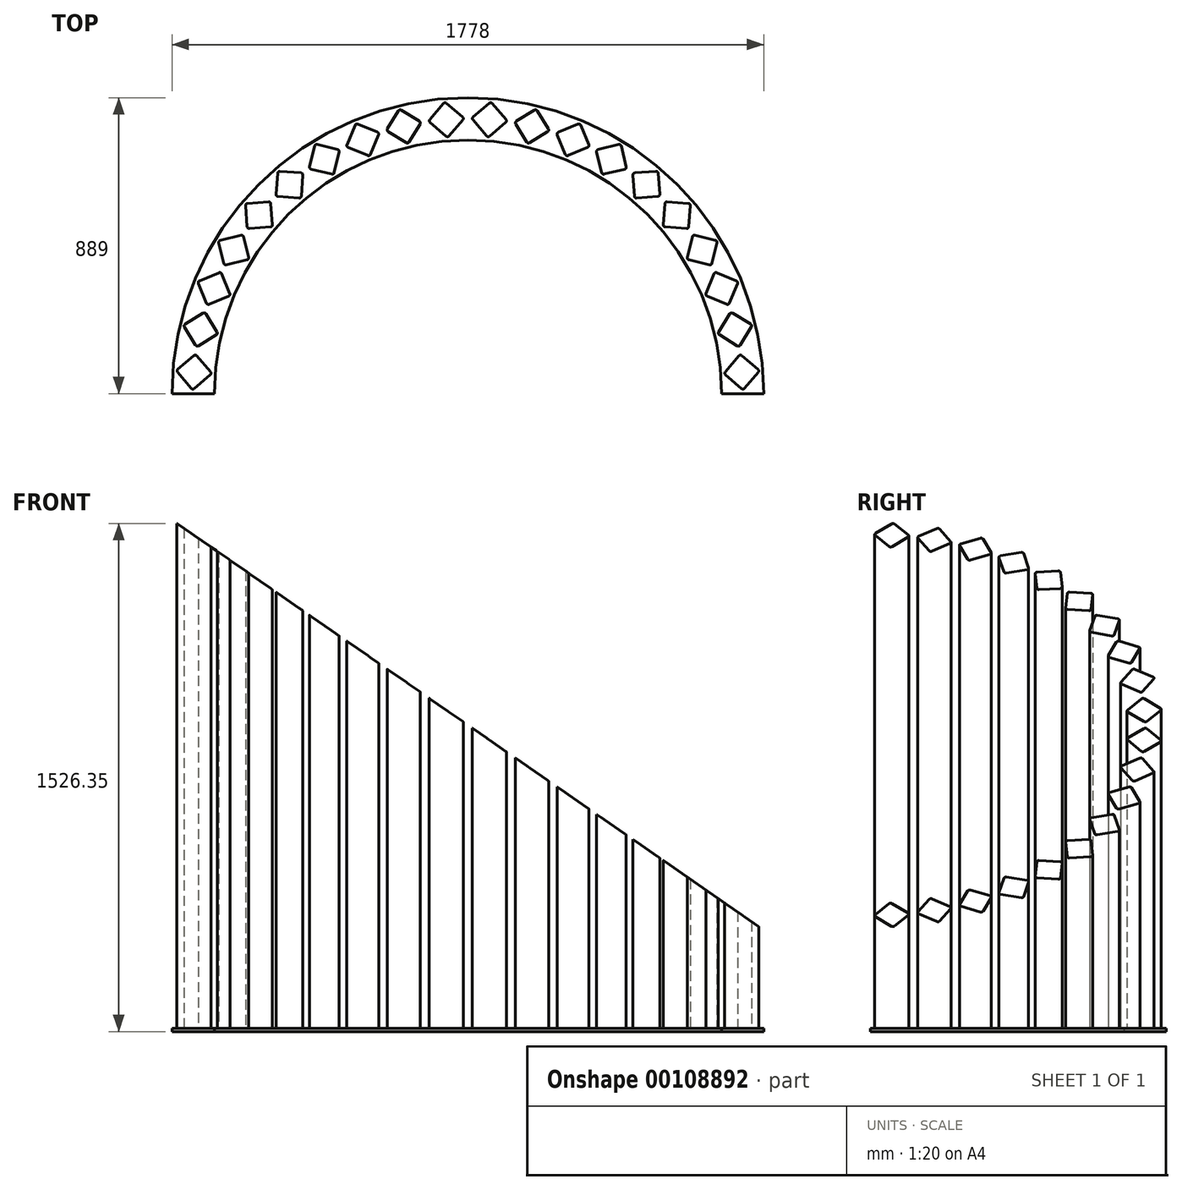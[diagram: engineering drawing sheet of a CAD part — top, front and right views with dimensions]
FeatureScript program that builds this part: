
annotation { "Feature Type Name" : "Feature", "Feature Type Description" : "" }
export const myFeature = defineFeature(function(context is Context, id is Id, definition is map)
    precondition{}
    {
        {
            var Q0;
            Q0=qCreatedBy(makeId("Top.planeOp"),FACE);
            var sketch = newSketch(context, id + "F0", { "sketchPlane" : qUnion([Q0])});
            skArc(sketch, "E0", {"start": v(889, 0) * mm, "mid": v(0, 889) * mm, "end": v(-889, 0) * mm});
            skArc(sketch, "E1", {"start": v(762, 0) * mm, "mid": v(0, 762) * mm, "end": v(-762, 0) * mm});
            skLineSegment(sketch, "E2", {"start": v(-889, 0) * mm, "end": v(-762, 0) * mm});
            skPoint(sketch, "E3.orphan", {"position": v(-1001.73, 0) * mm});
            skLineSegment(sketch, "E4.trimOffspring", {"start": v(762, 0) * mm, "end": v(889, 0) * mm});
            skSolve(sketch);
        }
        {
            var Q0;
            Q0 = qSketchRegion(id + "F0", true);
            extrude(context, id + "F1", {"entities" : qUnion([Q0]), "depth" : 9.52 * mm});
        }
        {
            var Q0;
            Q0=makeQuery(id+"F1.opExtrude","CAP_FACE",FACE,{"disambiguationData":[OSD([sQuery(id+"F0.wireOp",EDGE,"E0"),sQuery(id+"F0.wireOp",EDGE,"E1"),sQuery(id+"F0.wireOp",EDGE,"E2"),sQuery(id+"F0.wireOp",EDGE,"E4.trimOffspring")])],"isStart":false});
            var sketch = newSketch(context, id + "F2", { "sketchPlane" : qUnion([Q0])});
            skLineSegment(sketch, "E5", {"start": v(0, 0) * mm, "end": v(-951.47, 0) * mm, "construction": true});
            skLineSegment(sketch, "E6", {"start": v(0, 0) * mm, "end": v(-951.92, 74.92) * mm, "construction": true});
            skLineSegment(sketch, "E7", {"start": v(-720.22, 152.98) * mm, "end": v(-961.72, -53.27) * mm, "construction": true});
            skLineSegment(sketch, "E8", {"start": v(-871.84, 73.12) * mm, "end": v(-823.56, 114.36) * mm});
            skLineSegment(sketch, "E9", {"start": v(-822.35, 15.18) * mm, "end": v(-774.07, 56.42) * mm});
            skLineSegment(sketch, "E10", {"start": v(-814.6, 113.65) * mm, "end": v(-773.36, 65.37) * mm});
            skLineSegment(sketch, "E11", {"start": v(-872.55, 64.17) * mm, "end": v(-831.3, 15.88) * mm});
            skPoint(sketch, "E12", {"position": v(-822.96, 64.77) * mm});
            skArc(sketch, "E13.filletArc", {"start": v(-871.84, 73.12) * mm, "mid": v(-874.05, 68.79) * mm, "end": v(-872.55, 64.17) * mm});
            skArc(sketch, "E14.filletArc", {"start": v(-814.6, 113.65) * mm, "mid": v(-818.93, 115.86) * mm, "end": v(-823.56, 114.36) * mm});
            skArc(sketch, "E15.filletArc", {"start": v(-774.07, 56.42) * mm, "mid": v(-771.86, 60.75) * mm, "end": v(-773.36, 65.37) * mm});
            skArc(sketch, "E16.filletArc", {"start": v(-831.3, 15.88) * mm, "mid": v(-826.98, 13.67) * mm, "end": v(-822.35, 15.18) * mm});
            skLineSegment(sketch, "E17.9.3", {"start": v(-176.81, -755.71) * mm, "end": v(-176.81, -755.71) * mm});
            skLineSegment(sketch, "E17.9.5", {"start": v(-145.73, -818.59) * mm, "end": v(-145.73, -818.59) * mm});
            skLineSegment(sketch, "E17.10.3", {"start": v(-56.42, -774.07) * mm, "end": v(-56.42, -774.07) * mm});
            skLineSegment(sketch, "E17.12.3", {"start": v(185.55, -753.62) * mm, "end": v(185.55, -753.62) * mm});
            skLineSegment(sketch, "E17.12.7", {"start": v(199.87, -851.77) * mm, "end": v(199.87, -851.77) * mm});
            skLineSegment(sketch, "E17.14.5", {"start": v(475.78, -681.88) * mm, "end": v(475.78, -681.88) * mm});
            skLineSegment(sketch, "E17.21.0", {"start": v(872.55, 64.17) * mm, "end": v(831.3, 15.88) * mm});
            skArc(sketch, "E17.21.1", {"start": v(822.35, 15.18) * mm, "mid": v(826.98, 13.67) * mm, "end": v(831.3, 15.88) * mm});
            skLineSegment(sketch, "E17.21.2", {"start": v(822.35, 15.18) * mm, "end": v(774.07, 56.42) * mm});
            skArc(sketch, "E17.21.3", {"start": v(773.36, 65.37) * mm, "mid": v(771.86, 60.75) * mm, "end": v(774.07, 56.42) * mm});
            skLineSegment(sketch, "E17.21.4", {"start": v(814.6, 113.65) * mm, "end": v(773.36, 65.37) * mm});
            skArc(sketch, "E17.21.5", {"start": v(823.56, 114.36) * mm, "mid": v(818.93, 115.86) * mm, "end": v(814.6, 113.65) * mm});
            skLineSegment(sketch, "E17.21.6", {"start": v(871.84, 73.12) * mm, "end": v(823.56, 114.36) * mm});
            skArc(sketch, "E17.21.7", {"start": v(872.55, 64.17) * mm, "mid": v(874.05, 68.79) * mm, "end": v(871.84, 73.12) * mm});
            skLineSegment(sketch, "E17.22.0", {"start": v(851.77, 199.87) * mm, "end": v(818.59, 145.73) * mm});
            skArc(sketch, "E17.22.1", {"start": v(809.86, 143.63) * mm, "mid": v(814.66, 142.87) * mm, "end": v(818.59, 145.73) * mm});
            skLineSegment(sketch, "E17.22.2", {"start": v(809.86, 143.63) * mm, "end": v(755.71, 176.81) * mm});
            skArc(sketch, "E17.22.3", {"start": v(753.62, 185.55) * mm, "mid": v(752.86, 180.74) * mm, "end": v(755.71, 176.81) * mm});
            skLineSegment(sketch, "E17.22.4", {"start": v(786.8, 239.69) * mm, "end": v(753.62, 185.55) * mm});
            skArc(sketch, "E17.22.5", {"start": v(795.53, 241.78) * mm, "mid": v(790.73, 242.54) * mm, "end": v(786.8, 239.69) * mm});
            skLineSegment(sketch, "E17.22.6", {"start": v(849.67, 208.6) * mm, "end": v(795.53, 241.78) * mm});
            skArc(sketch, "E17.22.7", {"start": v(851.77, 199.87) * mm, "mid": v(852.53, 204.67) * mm, "end": v(849.67, 208.6) * mm});
            skLineSegment(sketch, "E17.23.0", {"start": v(810.01, 330.66) * mm, "end": v(785.71, 272) * mm});
            skArc(sketch, "E17.23.1", {"start": v(777.42, 268.56) * mm, "mid": v(782.28, 268.56) * mm, "end": v(785.71, 272) * mm});
            skLineSegment(sketch, "E17.23.2", {"start": v(777.42, 268.56) * mm, "end": v(718.75, 292.86) * mm});
            skArc(sketch, "E17.23.3", {"start": v(715.31, 301.15) * mm, "mid": v(715.31, 296.3) * mm, "end": v(718.75, 292.86) * mm});
            skLineSegment(sketch, "E17.23.4", {"start": v(739.61, 359.82) * mm, "end": v(715.31, 301.15) * mm});
            skArc(sketch, "E17.23.5", {"start": v(747.9, 363.26) * mm, "mid": v(743.05, 363.26) * mm, "end": v(739.61, 359.82) * mm});
            skLineSegment(sketch, "E17.23.6", {"start": v(806.58, 338.95) * mm, "end": v(747.9, 363.26) * mm});
            skArc(sketch, "E17.23.7", {"start": v(810.01, 330.66) * mm, "mid": v(810.01, 335.52) * mm, "end": v(806.58, 338.95) * mm});
            skLineSegment(sketch, "E17.24.0", {"start": v(748.31, 453.3) * mm, "end": v(733.49, 391.56) * mm});
            skArc(sketch, "E17.24.1", {"start": v(725.83, 386.86) * mm, "mid": v(730.63, 387.62) * mm, "end": v(733.49, 391.56) * mm});
            skLineSegment(sketch, "E17.24.2", {"start": v(725.83, 386.86) * mm, "end": v(664.09, 401.69) * mm});
            skArc(sketch, "E17.24.3", {"start": v(659.4, 409.34) * mm, "mid": v(660.16, 404.54) * mm, "end": v(664.09, 401.69) * mm});
            skLineSegment(sketch, "E17.24.4", {"start": v(674.22, 471.09) * mm, "end": v(659.4, 409.34) * mm});
            skArc(sketch, "E17.24.5", {"start": v(681.88, 475.78) * mm, "mid": v(677.08, 475.02) * mm, "end": v(674.22, 471.09) * mm});
            skLineSegment(sketch, "E17.24.6", {"start": v(743.62, 460.96) * mm, "end": v(681.88, 475.78) * mm});
            skArc(sketch, "E17.24.7", {"start": v(748.31, 453.3) * mm, "mid": v(747.55, 458.1) * mm, "end": v(743.62, 460.96) * mm});
            skLineSegment(sketch, "E17.25.0", {"start": v(668.19, 564.78) * mm, "end": v(663.2, 501.48) * mm});
            skArc(sketch, "E17.25.1", {"start": v(656.38, 495.65) * mm, "mid": v(661, 497.15) * mm, "end": v(663.2, 501.48) * mm});
            skLineSegment(sketch, "E17.25.2", {"start": v(656.38, 495.65) * mm, "end": v(593.07, 500.63) * mm});
            skArc(sketch, "E17.25.3", {"start": v(587.24, 507.46) * mm, "mid": v(588.74, 502.83) * mm, "end": v(593.07, 500.63) * mm});
            skLineSegment(sketch, "E17.25.4", {"start": v(592.22, 570.76) * mm, "end": v(587.24, 507.46) * mm});
            skArc(sketch, "E17.25.5", {"start": v(599.05, 576.6) * mm, "mid": v(594.43, 575.1) * mm, "end": v(592.22, 570.76) * mm});
            skLineSegment(sketch, "E17.25.6", {"start": v(662.36, 571.61) * mm, "end": v(599.05, 576.6) * mm});
            skArc(sketch, "E17.25.7", {"start": v(668.19, 564.78) * mm, "mid": v(666.69, 569.4) * mm, "end": v(662.36, 571.61) * mm});
            skLineSegment(sketch, "E17.26.0", {"start": v(571.61, 662.36) * mm, "end": v(576.6, 599.05) * mm});
            skArc(sketch, "E17.26.1", {"start": v(570.76, 592.22) * mm, "mid": v(575.1, 594.43) * mm, "end": v(576.6, 599.05) * mm});
            skLineSegment(sketch, "E17.26.2", {"start": v(570.76, 592.22) * mm, "end": v(507.46, 587.24) * mm});
            skArc(sketch, "E17.26.3", {"start": v(500.63, 593.07) * mm, "mid": v(502.83, 588.74) * mm, "end": v(507.46, 587.24) * mm});
            skLineSegment(sketch, "E17.26.4", {"start": v(495.65, 656.38) * mm, "end": v(500.63, 593.07) * mm});
            skArc(sketch, "E17.26.5", {"start": v(501.48, 663.2) * mm, "mid": v(497.15, 661) * mm, "end": v(495.65, 656.38) * mm});
            skLineSegment(sketch, "E17.26.6", {"start": v(564.78, 668.19) * mm, "end": v(501.48, 663.2) * mm});
            skArc(sketch, "E17.26.7", {"start": v(571.61, 662.36) * mm, "mid": v(569.4, 666.69) * mm, "end": v(564.78, 668.19) * mm});
            skLineSegment(sketch, "E17.27.0", {"start": v(460.96, 743.62) * mm, "end": v(475.78, 681.88) * mm});
            skArc(sketch, "E17.27.1", {"start": v(471.09, 674.22) * mm, "mid": v(475.02, 677.08) * mm, "end": v(475.78, 681.88) * mm});
            skLineSegment(sketch, "E17.27.2", {"start": v(471.09, 674.22) * mm, "end": v(409.34, 659.4) * mm});
            skArc(sketch, "E17.27.3", {"start": v(401.69, 664.09) * mm, "mid": v(404.54, 660.16) * mm, "end": v(409.34, 659.4) * mm});
            skLineSegment(sketch, "E17.27.4", {"start": v(386.86, 725.83) * mm, "end": v(401.69, 664.09) * mm});
            skArc(sketch, "E17.27.5", {"start": v(391.56, 733.49) * mm, "mid": v(387.62, 730.63) * mm, "end": v(386.86, 725.83) * mm});
            skLineSegment(sketch, "E17.27.6", {"start": v(453.3, 748.31) * mm, "end": v(391.56, 733.49) * mm});
            skArc(sketch, "E17.27.7", {"start": v(460.96, 743.62) * mm, "mid": v(458.1, 747.55) * mm, "end": v(453.3, 748.31) * mm});
            skLineSegment(sketch, "E17.28.0", {"start": v(338.95, 806.58) * mm, "end": v(363.26, 747.9) * mm});
            skArc(sketch, "E17.28.1", {"start": v(359.82, 739.61) * mm, "mid": v(363.26, 743.05) * mm, "end": v(363.26, 747.9) * mm});
            skLineSegment(sketch, "E17.28.2", {"start": v(359.82, 739.61) * mm, "end": v(301.15, 715.31) * mm});
            skArc(sketch, "E17.28.3", {"start": v(292.86, 718.75) * mm, "mid": v(296.3, 715.31) * mm, "end": v(301.15, 715.31) * mm});
            skLineSegment(sketch, "E17.28.4", {"start": v(268.56, 777.42) * mm, "end": v(292.86, 718.75) * mm});
            skArc(sketch, "E17.28.5", {"start": v(272, 785.71) * mm, "mid": v(268.56, 782.28) * mm, "end": v(268.56, 777.42) * mm});
            skLineSegment(sketch, "E17.28.6", {"start": v(330.66, 810.01) * mm, "end": v(272, 785.71) * mm});
            skArc(sketch, "E17.28.7", {"start": v(338.95, 806.58) * mm, "mid": v(335.52, 810.01) * mm, "end": v(330.66, 810.01) * mm});
            skLineSegment(sketch, "E17.29.0", {"start": v(208.6, 849.67) * mm, "end": v(241.78, 795.53) * mm});
            skArc(sketch, "E17.29.1", {"start": v(239.69, 786.8) * mm, "mid": v(242.54, 790.73) * mm, "end": v(241.78, 795.53) * mm});
            skLineSegment(sketch, "E17.29.2", {"start": v(239.69, 786.8) * mm, "end": v(185.55, 753.62) * mm});
            skArc(sketch, "E17.29.3", {"start": v(176.81, 755.71) * mm, "mid": v(180.74, 752.86) * mm, "end": v(185.55, 753.62) * mm});
            skLineSegment(sketch, "E17.29.4", {"start": v(143.63, 809.86) * mm, "end": v(176.81, 755.71) * mm});
            skArc(sketch, "E17.29.5", {"start": v(145.73, 818.59) * mm, "mid": v(142.87, 814.66) * mm, "end": v(143.63, 809.86) * mm});
            skLineSegment(sketch, "E17.29.6", {"start": v(199.87, 851.77) * mm, "end": v(145.73, 818.59) * mm});
            skArc(sketch, "E17.29.7", {"start": v(208.6, 849.67) * mm, "mid": v(204.67, 852.53) * mm, "end": v(199.87, 851.77) * mm});
            skLineSegment(sketch, "E17.30.0", {"start": v(73.12, 871.84) * mm, "end": v(114.36, 823.56) * mm});
            skArc(sketch, "E17.30.1", {"start": v(113.65, 814.6) * mm, "mid": v(115.86, 818.93) * mm, "end": v(114.36, 823.56) * mm});
            skLineSegment(sketch, "E17.30.2", {"start": v(113.65, 814.6) * mm, "end": v(65.37, 773.36) * mm});
            skArc(sketch, "E17.30.3", {"start": v(56.42, 774.07) * mm, "mid": v(60.75, 771.86) * mm, "end": v(65.37, 773.36) * mm});
            skLineSegment(sketch, "E17.30.4", {"start": v(15.18, 822.35) * mm, "end": v(56.42, 774.07) * mm});
            skArc(sketch, "E17.30.5", {"start": v(15.88, 831.3) * mm, "mid": v(13.67, 826.98) * mm, "end": v(15.18, 822.35) * mm});
            skLineSegment(sketch, "E17.30.6", {"start": v(64.17, 872.55) * mm, "end": v(15.88, 831.3) * mm});
            skArc(sketch, "E17.30.7", {"start": v(73.12, 871.84) * mm, "mid": v(68.79, 874.05) * mm, "end": v(64.17, 872.55) * mm});
            skLineSegment(sketch, "E17.31.0", {"start": v(-64.17, 872.55) * mm, "end": v(-15.88, 831.3) * mm});
            skArc(sketch, "E17.31.1", {"start": v(-15.18, 822.35) * mm, "mid": v(-13.67, 826.98) * mm, "end": v(-15.88, 831.3) * mm});
            skLineSegment(sketch, "E17.31.2", {"start": v(-15.18, 822.35) * mm, "end": v(-56.42, 774.07) * mm});
            skArc(sketch, "E17.31.3", {"start": v(-65.37, 773.36) * mm, "mid": v(-60.75, 771.86) * mm, "end": v(-56.42, 774.07) * mm});
            skLineSegment(sketch, "E17.31.4", {"start": v(-113.65, 814.6) * mm, "end": v(-65.37, 773.36) * mm});
            skArc(sketch, "E17.31.5", {"start": v(-114.36, 823.56) * mm, "mid": v(-115.86, 818.93) * mm, "end": v(-113.65, 814.6) * mm});
            skLineSegment(sketch, "E17.31.6", {"start": v(-73.12, 871.84) * mm, "end": v(-114.36, 823.56) * mm});
            skArc(sketch, "E17.31.7", {"start": v(-64.17, 872.55) * mm, "mid": v(-68.79, 874.05) * mm, "end": v(-73.12, 871.84) * mm});
            skLineSegment(sketch, "E17.32.0", {"start": v(-199.87, 851.77) * mm, "end": v(-145.73, 818.59) * mm});
            skArc(sketch, "E17.32.1", {"start": v(-143.63, 809.86) * mm, "mid": v(-142.87, 814.66) * mm, "end": v(-145.73, 818.59) * mm});
            skLineSegment(sketch, "E17.32.2", {"start": v(-143.63, 809.86) * mm, "end": v(-176.81, 755.71) * mm});
            skArc(sketch, "E17.32.3", {"start": v(-185.55, 753.62) * mm, "mid": v(-180.74, 752.86) * mm, "end": v(-176.81, 755.71) * mm});
            skLineSegment(sketch, "E17.32.4", {"start": v(-239.69, 786.8) * mm, "end": v(-185.55, 753.62) * mm});
            skArc(sketch, "E17.32.5", {"start": v(-241.78, 795.53) * mm, "mid": v(-242.54, 790.73) * mm, "end": v(-239.69, 786.8) * mm});
            skLineSegment(sketch, "E17.32.6", {"start": v(-208.6, 849.67) * mm, "end": v(-241.78, 795.53) * mm});
            skArc(sketch, "E17.32.7", {"start": v(-199.87, 851.77) * mm, "mid": v(-204.67, 852.53) * mm, "end": v(-208.6, 849.67) * mm});
            skLineSegment(sketch, "E17.33.0", {"start": v(-330.66, 810.01) * mm, "end": v(-272, 785.71) * mm});
            skArc(sketch, "E17.33.1", {"start": v(-268.56, 777.42) * mm, "mid": v(-268.56, 782.28) * mm, "end": v(-272, 785.71) * mm});
            skLineSegment(sketch, "E17.33.2", {"start": v(-268.56, 777.42) * mm, "end": v(-292.86, 718.75) * mm});
            skArc(sketch, "E17.33.3", {"start": v(-301.15, 715.31) * mm, "mid": v(-296.3, 715.31) * mm, "end": v(-292.86, 718.75) * mm});
            skLineSegment(sketch, "E17.33.4", {"start": v(-359.82, 739.61) * mm, "end": v(-301.15, 715.31) * mm});
            skArc(sketch, "E17.33.5", {"start": v(-363.26, 747.9) * mm, "mid": v(-363.26, 743.05) * mm, "end": v(-359.82, 739.61) * mm});
            skLineSegment(sketch, "E17.33.6", {"start": v(-338.95, 806.58) * mm, "end": v(-363.26, 747.9) * mm});
            skArc(sketch, "E17.33.7", {"start": v(-330.66, 810.01) * mm, "mid": v(-335.52, 810.01) * mm, "end": v(-338.95, 806.58) * mm});
            skLineSegment(sketch, "E17.34.0", {"start": v(-453.3, 748.31) * mm, "end": v(-391.56, 733.49) * mm});
            skArc(sketch, "E17.34.1", {"start": v(-386.86, 725.83) * mm, "mid": v(-387.62, 730.63) * mm, "end": v(-391.56, 733.49) * mm});
            skLineSegment(sketch, "E17.34.2", {"start": v(-386.86, 725.83) * mm, "end": v(-401.69, 664.09) * mm});
            skArc(sketch, "E17.34.3", {"start": v(-409.34, 659.4) * mm, "mid": v(-404.54, 660.16) * mm, "end": v(-401.69, 664.09) * mm});
            skLineSegment(sketch, "E17.34.4", {"start": v(-471.09, 674.22) * mm, "end": v(-409.34, 659.4) * mm});
            skArc(sketch, "E17.34.5", {"start": v(-475.78, 681.88) * mm, "mid": v(-475.02, 677.08) * mm, "end": v(-471.09, 674.22) * mm});
            skLineSegment(sketch, "E17.34.6", {"start": v(-460.96, 743.62) * mm, "end": v(-475.78, 681.88) * mm});
            skArc(sketch, "E17.34.7", {"start": v(-453.3, 748.31) * mm, "mid": v(-458.1, 747.55) * mm, "end": v(-460.96, 743.62) * mm});
            skLineSegment(sketch, "E17.35.0", {"start": v(-564.78, 668.19) * mm, "end": v(-501.48, 663.2) * mm});
            skArc(sketch, "E17.35.1", {"start": v(-495.65, 656.38) * mm, "mid": v(-497.15, 661) * mm, "end": v(-501.48, 663.2) * mm});
            skLineSegment(sketch, "E17.35.2", {"start": v(-495.65, 656.38) * mm, "end": v(-500.63, 593.07) * mm});
            skArc(sketch, "E17.35.3", {"start": v(-507.46, 587.24) * mm, "mid": v(-502.83, 588.74) * mm, "end": v(-500.63, 593.07) * mm});
            skLineSegment(sketch, "E17.35.4", {"start": v(-570.76, 592.22) * mm, "end": v(-507.46, 587.24) * mm});
            skArc(sketch, "E17.35.5", {"start": v(-576.6, 599.05) * mm, "mid": v(-575.1, 594.43) * mm, "end": v(-570.76, 592.22) * mm});
            skLineSegment(sketch, "E17.35.6", {"start": v(-571.61, 662.36) * mm, "end": v(-576.6, 599.05) * mm});
            skArc(sketch, "E17.35.7", {"start": v(-564.78, 668.19) * mm, "mid": v(-569.4, 666.69) * mm, "end": v(-571.61, 662.36) * mm});
            skLineSegment(sketch, "E17.36.0", {"start": v(-662.36, 571.61) * mm, "end": v(-599.05, 576.6) * mm});
            skArc(sketch, "E17.36.1", {"start": v(-592.22, 570.76) * mm, "mid": v(-594.43, 575.1) * mm, "end": v(-599.05, 576.6) * mm});
            skLineSegment(sketch, "E17.36.2", {"start": v(-592.22, 570.76) * mm, "end": v(-587.24, 507.46) * mm});
            skArc(sketch, "E17.36.3", {"start": v(-593.07, 500.63) * mm, "mid": v(-588.74, 502.83) * mm, "end": v(-587.24, 507.46) * mm});
            skLineSegment(sketch, "E17.36.4", {"start": v(-656.38, 495.65) * mm, "end": v(-593.07, 500.63) * mm});
            skArc(sketch, "E17.36.5", {"start": v(-663.2, 501.48) * mm, "mid": v(-661, 497.15) * mm, "end": v(-656.38, 495.65) * mm});
            skLineSegment(sketch, "E17.36.6", {"start": v(-668.19, 564.78) * mm, "end": v(-663.2, 501.48) * mm});
            skArc(sketch, "E17.36.7", {"start": v(-662.36, 571.61) * mm, "mid": v(-666.69, 569.4) * mm, "end": v(-668.19, 564.78) * mm});
            skLineSegment(sketch, "E17.37.0", {"start": v(-743.62, 460.96) * mm, "end": v(-681.88, 475.78) * mm});
            skArc(sketch, "E17.37.1", {"start": v(-674.22, 471.09) * mm, "mid": v(-677.08, 475.02) * mm, "end": v(-681.88, 475.78) * mm});
            skLineSegment(sketch, "E17.37.2", {"start": v(-674.22, 471.09) * mm, "end": v(-659.4, 409.34) * mm});
            skArc(sketch, "E17.37.3", {"start": v(-664.09, 401.69) * mm, "mid": v(-660.16, 404.54) * mm, "end": v(-659.4, 409.34) * mm});
            skLineSegment(sketch, "E17.37.4", {"start": v(-725.83, 386.86) * mm, "end": v(-664.09, 401.69) * mm});
            skArc(sketch, "E17.37.5", {"start": v(-733.49, 391.56) * mm, "mid": v(-730.63, 387.62) * mm, "end": v(-725.83, 386.86) * mm});
            skLineSegment(sketch, "E17.37.6", {"start": v(-748.31, 453.3) * mm, "end": v(-733.49, 391.56) * mm});
            skArc(sketch, "E17.37.7", {"start": v(-743.62, 460.96) * mm, "mid": v(-747.55, 458.1) * mm, "end": v(-748.31, 453.3) * mm});
            skLineSegment(sketch, "E17.38.0", {"start": v(-806.58, 338.95) * mm, "end": v(-747.9, 363.26) * mm});
            skArc(sketch, "E17.38.1", {"start": v(-739.61, 359.82) * mm, "mid": v(-743.05, 363.26) * mm, "end": v(-747.9, 363.26) * mm});
            skLineSegment(sketch, "E17.38.2", {"start": v(-739.61, 359.82) * mm, "end": v(-715.31, 301.15) * mm});
            skArc(sketch, "E17.38.3", {"start": v(-718.75, 292.86) * mm, "mid": v(-715.31, 296.3) * mm, "end": v(-715.31, 301.15) * mm});
            skLineSegment(sketch, "E17.38.4", {"start": v(-777.42, 268.56) * mm, "end": v(-718.75, 292.86) * mm});
            skArc(sketch, "E17.38.5", {"start": v(-785.71, 272) * mm, "mid": v(-782.28, 268.56) * mm, "end": v(-777.42, 268.56) * mm});
            skLineSegment(sketch, "E17.38.6", {"start": v(-810.01, 330.66) * mm, "end": v(-785.71, 272) * mm});
            skArc(sketch, "E17.38.7", {"start": v(-806.58, 338.95) * mm, "mid": v(-810.01, 335.52) * mm, "end": v(-810.01, 330.66) * mm});
            skPoint(sketch, "E17.center", {"position": v(0, 0) * mm});
            skLineSegment(sketch, "E18.1.39.0", {"start": v(-849.67, 208.6) * mm, "end": v(-795.53, 241.78) * mm});
            skArc(sketch, "E18.3.39.0", {"start": v(-786.8, 239.69) * mm, "mid": v(-790.73, 242.54) * mm, "end": v(-795.53, 241.78) * mm});
            skLineSegment(sketch, "E18.7.39.0", {"start": v(-786.8, 239.69) * mm, "end": v(-753.62, 185.55) * mm});
            skArc(sketch, "E18.10.39.0", {"start": v(-755.71, 176.81) * mm, "mid": v(-752.86, 180.74) * mm, "end": v(-753.62, 185.55) * mm});
            skLineSegment(sketch, "E18.14.39.0", {"start": v(-809.86, 143.63) * mm, "end": v(-755.71, 176.81) * mm});
            skArc(sketch, "E18.17.39.0", {"start": v(-818.59, 145.73) * mm, "mid": v(-814.66, 142.87) * mm, "end": v(-809.86, 143.63) * mm});
            skLineSegment(sketch, "E18.21.39.0", {"start": v(-851.77, 199.87) * mm, "end": v(-818.59, 145.73) * mm});
            skArc(sketch, "E18.24.39.0", {"start": v(-849.67, 208.6) * mm, "mid": v(-852.53, 204.67) * mm, "end": v(-851.77, 199.87) * mm});
            skPoint(sketch, "E19.orphan", {"position": v(-831.3, -15.88) * mm});
            skArc(sketch, "E20.trimOffspring", {"start": v(825.39, 13.75) * mm, "mid": v(-6.88, 825.47) * mm, "end": v(-825.5, 0) * mm, "construction": true});
            skPoint(sketch, "E21.orphan", {"position": v(-747.9, -363.26) * mm});
            skPoint(sketch, "E22.orphan", {"position": v(-185.55, -753.62) * mm});
            skPoint(sketch, "E23.orphan", {"position": v(-143.63, -809.86) * mm});
            skPoint(sketch, "E24.orphan", {"position": v(-65.37, -773.36) * mm});
            skPoint(sketch, "E25.orphan", {"position": v(176.81, -755.71) * mm});
            skPoint(sketch, "E26.orphan", {"position": v(208.6, -849.67) * mm});
            skPoint(sketch, "E27.orphan", {"position": v(471.09, -674.22) * mm});
            skPoint(sketch, "E28", {"position": v(-13.67, 826.98) * mm});
            skPoint(sketch, "E29", {"position": v(13.65, 826.9) * mm});
            skSolve(sketch);
        }
        {
            var Q0;
            Q0 = qSketchRegion(id + "F2", true);
            extrude(context, id + "F3", {"entities" : qUnion([Q0]), "operationType" : NewBodyOperationType.ADD, "depth" : 1524 * mm});
        }
        {
            var Q0;
            Q0=qCreatedBy(makeId("Front.planeOp"),FACE);
            var sketch = newSketch(context, id + "F4", { "sketchPlane" : qUnion([Q0])});
            skLineSegment(sketch, "E30", {"start": v(-991.98, 1536.7) * mm, "end": v(1002.76, 1536.7) * mm, "construction": true});
            skLineSegment(sketch, "E31", {"start": v(-889, 1603.91) * mm, "end": v(-889, -208.72) * mm, "construction": true});
            skLineSegment(sketch, "E32", {"start": v(889, 1597.82) * mm, "end": v(889, -312.3) * mm, "construction": true});
            skLineSegment(sketch, "E33", {"start": v(-1191.5, 304.8) * mm, "end": v(1595.98, 304.8) * mm, "construction": true});
            skPoint(sketch, "E34", {"position": v(-889, 1536.7) * mm});
            skPoint(sketch, "E35", {"position": v(889, 304.8) * mm});
            skLineSegment(sketch, "E36", {"start": v(-889, 1536.7) * mm, "end": v(889, 304.8) * mm});
            skLineSegment(sketch, "E37", {"start": v(889, 304.8) * mm, "end": v(889, 1536.7) * mm});
            skLineSegment(sketch, "E38", {"start": v(889, 1536.7) * mm, "end": v(-889, 1536.7) * mm});
            skSolve(sketch);
        }
        {
            var Q0;
            Q0 = qSketchRegion(id + "F4", true);
            extrude(context, id + "F5", {"entities" : qUnion([Q0]), "operationType" : NewBodyOperationType.REMOVE, "endBound" : BoundingType.THROUGH_ALL, "oppositeDirection" : true, "depth" : 25.4 * mm});
        }
    });
